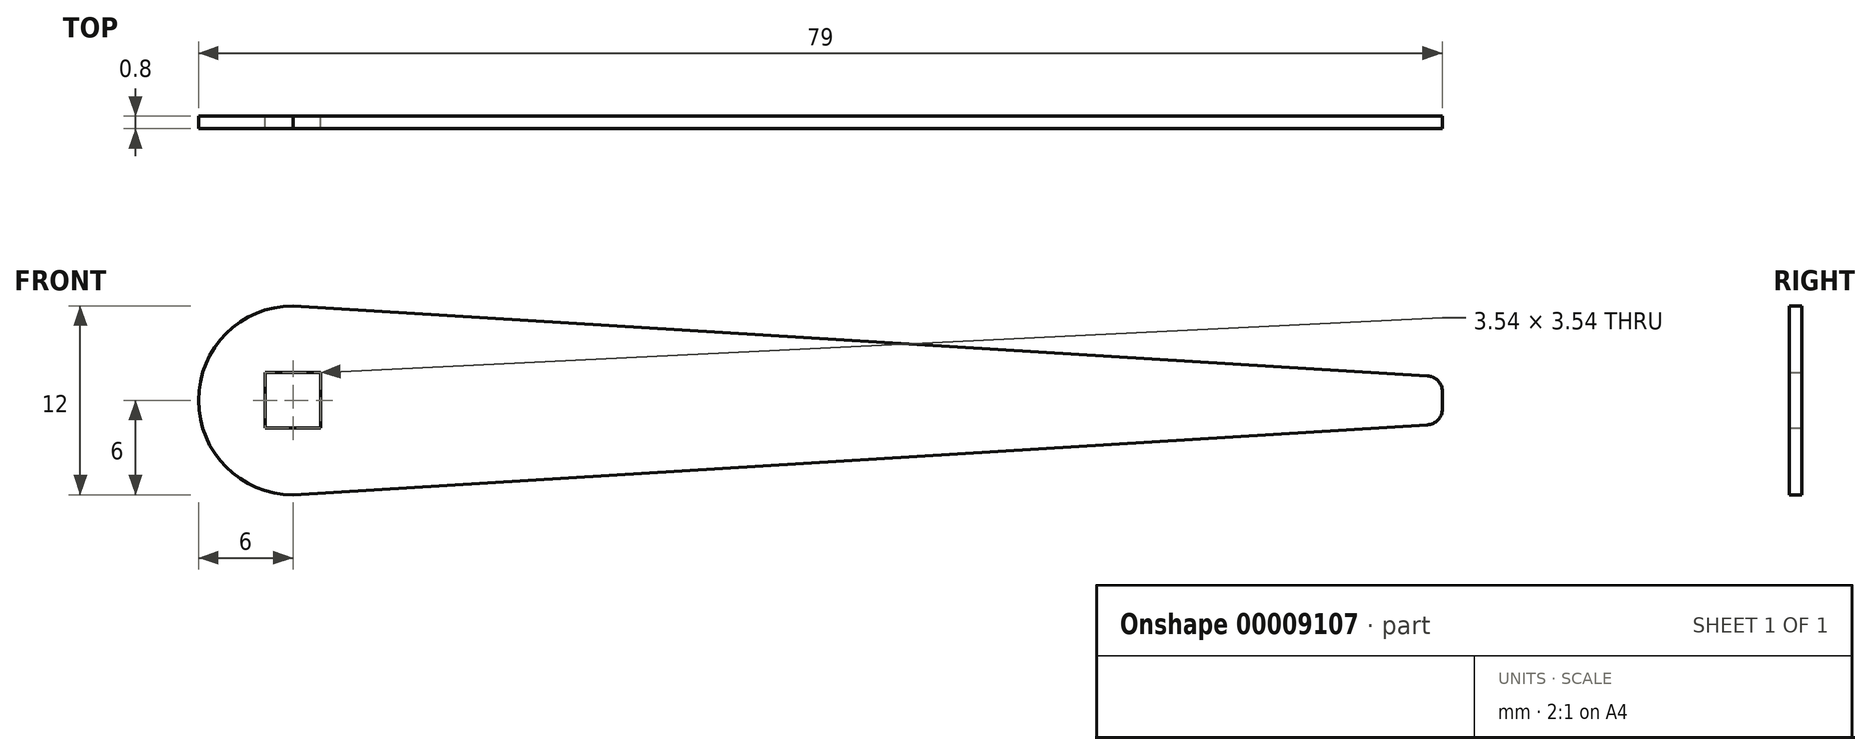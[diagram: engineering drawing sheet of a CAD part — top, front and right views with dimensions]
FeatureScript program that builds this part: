
annotation { "Feature Type Name" : "Feature", "Feature Type Description" : "" }
export const myFeature = defineFeature(function(context is Context, id is Id, definition is map)
    precondition{}
    {
        {
            var Q0;
            Q0=qCreatedBy(makeId("Front.planeOp"),FACE);
            var sketch = newSketch(context, id + "F0", { "sketchPlane" : qUnion([Q0])});
            skLineSegment(sketch, "E0.rect.bottom", {"start": v(1.77, 1.77) * mm, "end": v(-1.77, 1.77) * mm});
            skLineSegment(sketch, "E0.rect.top", {"start": v(1.77, -1.77) * mm, "end": v(-1.77, -1.77) * mm});
            skLineSegment(sketch, "E0.rect.left", {"start": v(1.77, 1.77) * mm, "end": v(1.77, -1.77) * mm});
            skLineSegment(sketch, "E0.rect.right", {"start": v(-1.77, 1.77) * mm, "end": v(-1.77, -1.77) * mm});
            skPoint(sketch, "E0.rect.middle", {"position": v(0, 0) * mm});
            skCircle(sketch, "E1", {"center": v(0, 0) * mm, "radius": 6 * mm});
            skLineSegment(sketch, "E2", {"start": v(0, 6) * mm, "end": v(73, 1.5) * mm});
            skLineSegment(sketch, "E3", {"start": v(73, 1.5) * mm, "end": v(73, 0) * mm});
            skLineSegment(sketch, "E4.MirrorCS", {"start": v(0, -6) * mm, "end": v(73, -1.5) * mm});
            skLineSegment(sketch, "E5.MirrorCS", {"start": v(73, -1.5) * mm, "end": v(73, 0) * mm});
            skSolve(sketch);
        }
        {
            var Q0;
            Q0=makeQuery(id+"F0.imprint","IMPRINT",FACE,{"disambiguationData":[TD([[makeQuery(id+"F0.imprint","IMPRINT",EDGE,{"derivedFrom":sQuery(id+"F0.wireOp",EDGE,"E0.rect.bottom")}),-1.0]])]});
            var Q1;
            {var subQ1=sQuery(id+"F0.wireOp",EDGE,"E2");Q1=makeQuery(id+"F0.imprint","IMPRINT",FACE,{"disambiguationData":[TD([[makeQuery(id+"F0.imprint","IMPRINT",EDGE,{"derivedFrom":subQ1}),-1.0]])]});}
            extrude(context, id + "F1", {"entities" : qUnion([Q0, Q1]), "depth" : 0.8 * mm});
        }
        {
            var Q0;
            Q0=makeQuery(id+"F1.opExtrude","CAP_FACE",FACE,{"disambiguationData":[OSD([sQuery(id+"F0.wireOp",EDGE,"E0.rect.bottom"),sQuery(id+"F0.wireOp",EDGE,"E0.rect.top"),sQuery(id+"F0.wireOp",EDGE,"E0.rect.left"),sQuery(id+"F0.wireOp",EDGE,"E0.rect.right"),sQuery(id+"F0.wireOp",EDGE,"E1"),sQuery(id+"F0.wireOp",EDGE,"E2"),sQuery(id+"F0.wireOp",EDGE,"E3"),sQuery(id+"F0.wireOp",EDGE,"E4.MirrorCS"),sQuery(id+"F0.wireOp",EDGE,"E5.MirrorCS")])],"isStart":false});
            var sketch = newSketch(context, id + "F2", { "sketchPlane" : qUnion([Q0])});
            skLineSegment(sketch, "E6.0.0", {"start": v(73, 1.5) * mm, "end": v(0, 6) * mm});
            skArc(sketch, "E6.0.1", {"start": v(0, 6) * mm, "mid": v(-6, 0) * mm, "end": v(0, -6) * mm});
            skLineSegment(sketch, "E6.0.2", {"start": v(0, -6) * mm, "end": v(73, -1.5) * mm});
            skLineSegment(sketch, "E6.0.3", {"start": v(73, -1.5) * mm, "end": v(73, 1.5) * mm});
            skLineSegment(sketch, "E7.0", {"start": v(48.57, 0) * mm, "end": v(-0.18, 3) * mm});
            skLineSegment(sketch, "E7.1", {"start": v(-0.18, -3) * mm, "end": v(48.57, 0) * mm});
            skCircle(sketch, "E8", {"center": v(0, 0) * mm, "radius": 7.5 * mm});
            skSolve(sketch);
        }
        {
            var Q0;
            Q0=makeQuery(id+"Fjm3f5GU0jwRa2O_1.boolean.opBoolean","COPY",EDGE,{"derivedFrom":makeQuery(id+"Fjm3f5GU0jwRa2O_1.opExtrude","SWEPT_EDGE",EDGE,{"disambiguationData":[OSD([sQuery(id+"F2.wireOp",EDGE,"E7.0"),sQuery(id+"F2.wireOp",EDGE,"E8")])]})});
            var Q1;
            Q1=makeQuery(id+"Fjm3f5GU0jwRa2O_1.boolean.opBoolean","COPY",EDGE,{"derivedFrom":makeQuery(id+"Fjm3f5GU0jwRa2O_1.opExtrude","SWEPT_EDGE",EDGE,{"disambiguationData":[OSD([sQuery(id+"F2.wireOp",EDGE,"E7.1"),sQuery(id+"F2.wireOp",EDGE,"E8")])]})});
            var Q2;
            Q2=makeQuery(id+"Fjm3f5GU0jwRa2O_1.boolean.opBoolean","COPY",EDGE,{"derivedFrom":makeQuery(id+"Fjm3f5GU0jwRa2O_1.opExtrude","SWEPT_EDGE",EDGE,{"disambiguationData":[OSD([sQuery(id+"F2.wireOp",EDGE,"E7.0"),sQuery(id+"F2.wireOp",EDGE,"E7.1")])]})});
            var Q3;
            Q3=makeQuery(id+"F1.opExtrude","SWEPT_EDGE",EDGE,{"disambiguationData":[OSD([sQuery(id+"F0.wireOp",EDGE,"E2"),sQuery(id+"F0.wireOp",EDGE,"E3")])]});
            var Q4;
            Q4=makeQuery(id+"F1.opExtrude","SWEPT_EDGE",EDGE,{"disambiguationData":[OSD([sQuery(id+"F0.wireOp",EDGE,"E4.MirrorCS"),sQuery(id+"F0.wireOp",EDGE,"E5.MirrorCS")])]});
            fillet(context, id + "F3", {"entities" : qUnion([Q0, Q1, Q2, Q3, Q4]), "radius" : 1 * mm, "tangentPropagation" : true, "allowEdgeOverflow" : false});
        }
    });
